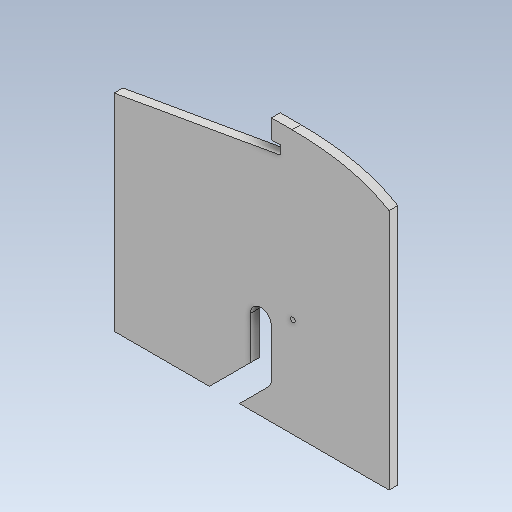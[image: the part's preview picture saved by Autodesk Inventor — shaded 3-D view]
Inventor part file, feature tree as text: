
AUTODESK INVENTOR PART (.ipt)
format: ipt  version: 2020 (Build 240168000, 168)  size: 130,048 bytes
history: native  units: mm
features: other x20, extrude x1, sketch x1
ambient origin geometry x8: Origin, YZ Plane, XZ Plane, XY Plane, X Axis, Y Axis, Z Axis, Center Point
bodies: Body1 (feature_tree)
feature tree (22):
  other  "Sólido1"
  extrude  "Extrusão1"  Depth=10.0mm
  sketch  "Esboço1"  dims[d0=3.0mm d1=0.0mm d3=10.0mm d5=7.0mm d6=7.0mm d7=3.0mm]
  other  "Referência1"
  other  "Referência2"
  other  "Referência3"
  other  "Referência4"
  other  "Referência5"
  other  "Referência6"
  other  "Referência7"
  other  "Referência8"
  other  "Referência9"
  other  "Referência10"
  other  "Referência11"
  other  "Referência13"
  other  "<userpath>\Desktop\rabo\3d\ela.iam"
  other  "ela.iam"
  other  "PCB:1"
  other  "basesinha:1"
  other  "Component2_6:3"
  other  "Component2_32:2"
  other  "microservoSG90_MIR:1"
